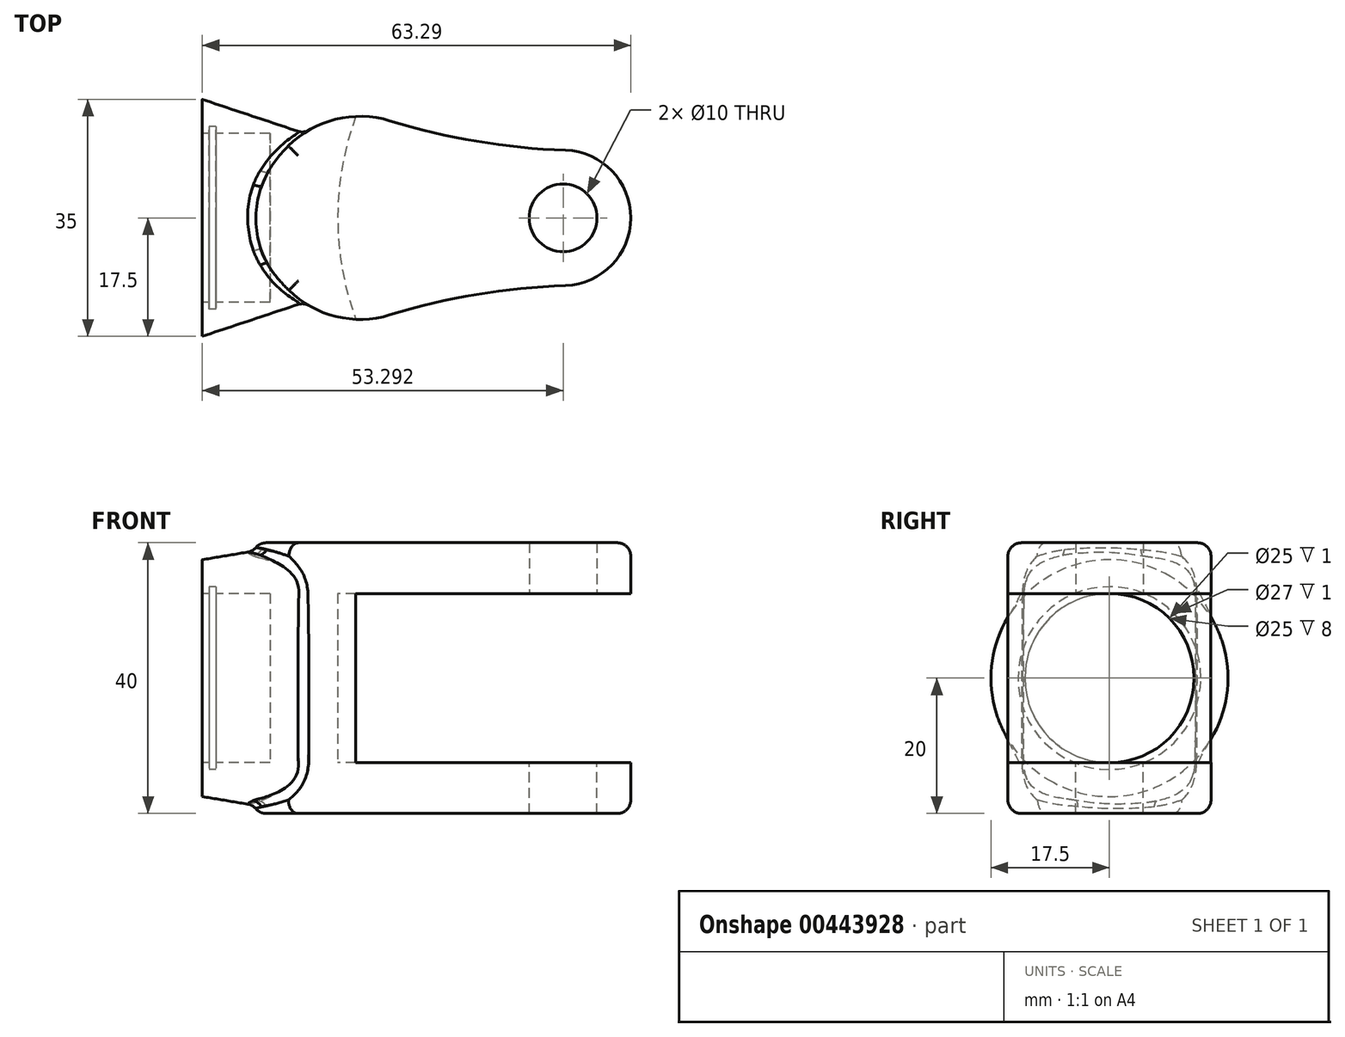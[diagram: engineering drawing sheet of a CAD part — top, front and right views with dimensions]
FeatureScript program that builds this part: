
annotation { "Feature Type Name" : "Feature", "Feature Type Description" : "" }
export const myFeature = defineFeature(function(context is Context, id is Id, definition is map)
    precondition{}
    {
        {
            var Q0;
            Q0=qCreatedBy(makeId("Right.planeOp"),FACE);
            var sketch = newSketch(context, id + "F0", { "sketchPlane" : qUnion([Q0])});
            skCircle(sketch, "E0", {"center": v(0, 0) * mm, "radius": 17.5 * mm});
            skSolve(sketch);
        }
        {
            var Q0;
            Q0=qCreatedBy(makeId("Right.planeOp"),FACE);
            cPlane(context, id + "F1", {"entities" : qUnion([Q0]), "cplaneType" : CPlaneType.OFFSET, "offset" : 15 * mm, "width" : 150 * mm, "height" : 150 * mm});
        }
        {
            var Q0;
            Q0=qCreatedBy(id+"F1.planeOp",FACE);
            var sketch = newSketch(context, id + "F2", { "sketchPlane" : qUnion([Q0])});
            skLineSegment(sketch, "E1.bottom", {"start": v(5, -20) * mm, "end": v(-5, -20) * mm});
            skLineSegment(sketch, "E1.top", {"start": v(5, 20) * mm, "end": v(-5, 20) * mm});
            skLineSegment(sketch, "E1.left", {"start": v(12.5, -12.5) * mm, "end": v(12.5, 12.5) * mm});
            skLineSegment(sketch, "E1.right", {"start": v(-12.5, -12.5) * mm, "end": v(-12.5, 12.5) * mm});
            skPoint(sketch, "E1.middle", {"position": v(0, 0) * mm});
            skPoint(sketch, "E2.visualSharp", {"position": v(-12.5, 20) * mm});
            skArc(sketch, "E2.filletArc", {"start": v(-5, 20) * mm, "mid": v(-10.3, 17.8) * mm, "end": v(-12.5, 12.5) * mm});
            skPoint(sketch, "E3.visualSharp", {"position": v(12.5, 20) * mm});
            skArc(sketch, "E3.filletArc", {"start": v(12.5, 12.5) * mm, "mid": v(10.3, 17.8) * mm, "end": v(5, 20) * mm});
            skPoint(sketch, "E4.visualSharp", {"position": v(12.5, -20) * mm});
            skArc(sketch, "E4.filletArc", {"start": v(5, -20) * mm, "mid": v(10.3, -17.8) * mm, "end": v(12.5, -12.5) * mm});
            skPoint(sketch, "E5.visualSharp", {"position": v(-12.5, -20) * mm});
            skArc(sketch, "E5.filletArc", {"start": v(-12.5, -12.5) * mm, "mid": v(-10.3, -17.8) * mm, "end": v(-5, -20) * mm});
            skSolve(sketch);
        }
        {
            var Q0;
            Q0 = qSketchRegion(id + "F2", true);
            var Q1;
            Q1 = qSketchRegion(id + "F0", true);
            loft(context, id + "F3", {"sheetProfilesArray" : [{ "sheetProfileEntities" : qUnion([Q0]) }, { "sheetProfileEntities" : qUnion([Q1]) }]});
        }
        {
            var Q0;
            Q0=qCreatedBy(makeId("Top.planeOp"),FACE);
            var sketch = newSketch(context, id + "F4", { "sketchPlane" : qUnion([Q0])});
            skCircle(sketch, "E6", {"center": v(23.3, 0) * mm, "radius": 15 * mm});
            skCircle(sketch, "E7", {"center": v(53.3, 0) * mm, "radius": 10 * mm});
            skArc(sketch, "E8", {"start": v(27.7, 14.34) * mm, "mid": v(40.52, 11.31) * mm, "end": v(53.63, 10) * mm});
            skArc(sketch, "E9.MirrorCS", {"start": v(27.7, -14.34) * mm, "mid": v(40.52, -11.31) * mm, "end": v(53.63, -10) * mm});
            skSolve(sketch);
        }
        {
            var Q0;
            Q0 = qSketchRegion(id + "F4", true);
            extrude(context, id + "F5", {"entities" : qUnion([Q0]), "operationType" : NewBodyOperationType.ADD, "endBound" : BoundingType.SYMMETRIC, "depth" : 40 * mm});
        }
        {
            var Q0;
            Q0=qCreatedBy(makeId("Front.planeOp"),FACE);
            var sketch = newSketch(context, id + "F6", { "sketchPlane" : qUnion([Q0])});
            skLineSegment(sketch, "E10.bottom", {"start": v(20, 12.5) * mm, "end": v(63.38, 12.5) * mm});
            skLineSegment(sketch, "E10.top", {"start": v(20, -12.5) * mm, "end": v(63.38, -12.5) * mm});
            skLineSegment(sketch, "E10.left", {"start": v(20, 12.5) * mm, "end": v(20, -12.5) * mm});
            skLineSegment(sketch, "E10.right", {"start": v(63.38, 12.5) * mm, "end": v(63.38, -12.5) * mm});
            skSolve(sketch);
        }
        {
            var Q0;
            Q0 = qSketchRegion(id + "F6", true);
            var Q1;
            Q1=sQuery(id+"F6.wireOp",EDGE,"E10.right");
            revolve(context, id + "F7", {"operationType" : NewBodyOperationType.REMOVE, "entities" : qUnion([Q0]), "axis" : qUnion([Q1]), "revolveType" : RevolveType.FULL, "oppositeDirection" : true});
        }
        {
            var Q0;
            Q0=makeQuery(id+"F3.opLoft","CAP_FACE",FACE,{"disambiguationData":[OSD([makeQuery(id+"F0.imprint","IMPRINT",FACE,{"disambiguationData":[TD([[makeQuery(id+"F0.imprint","IMPRINT",EDGE,{"derivedFrom":sQuery(id+"F0.wireOp",EDGE,"E0")}),1.0]])]})])],"isStart":true});
            var sketch = newSketch(context, id + "F8", { "sketchPlane" : qUnion([Q0])});
            skCircle(sketch, "E11", {"center": v(0, 0) * mm, "radius": 12.5 * mm});
            skSolve(sketch);
        }
        {
            var Q0;
            Q0 = qSketchRegion(id + "F8", true);
            extrude(context, id + "F9", {"entities" : qUnion([Q0]), "operationType" : NewBodyOperationType.REMOVE, "oppositeDirection" : true, "depth" : 10 * mm});
        }
        {
            var Q0;
            Q0=makeQuery(id+"F3.opLoft","CAP_FACE",FACE,{"disambiguationData":[OSD([makeQuery(id+"F0.imprint","IMPRINT",FACE,{"disambiguationData":[TD([[makeQuery(id+"F0.imprint","IMPRINT",EDGE,{"derivedFrom":sQuery(id+"F0.wireOp",EDGE,"E0")}),1.0]])]})])],"isStart":true});
            cPlane(context, id + "F10", {"entities" : qUnion([Q0]), "cplaneType" : CPlaneType.OFFSET, "offset" : 1 * mm, "oppositeDirection" : true, "width" : 150 * mm, "height" : 150 * mm});
        }
        {
            var Q0;
            Q0=qCreatedBy(id+"F10.planeOp",FACE);
            var sketch = newSketch(context, id + "F11", { "sketchPlane" : qUnion([Q0])});
            skCircle(sketch, "E12.0", {"center": v(0, 0) * mm, "radius": 13.5 * mm});
            skSolve(sketch);
        }
        {
            var Q0;
            Q0 = qSketchRegion(id + "F11", true);
            extrude(context, id + "F12", {"entities" : qUnion([Q0]), "operationType" : NewBodyOperationType.REMOVE, "oppositeDirection" : true, "depth" : 1 * mm});
        }
        {
            var Q0;
            Q0=qCreatedBy(makeId("Top.planeOp"),FACE);
            var sketch = newSketch(context, id + "F13", { "sketchPlane" : qUnion([Q0])});
            skCircle(sketch, "E13", {"center": v(53.3, 0) * mm, "radius": 5 * mm});
            skSolve(sketch);
        }
        {
            var Q0;
            Q0 = qSketchRegion(id + "F13", true);
            extrude(context, id + "F14", {"entities" : qUnion([Q0]), "operationType" : NewBodyOperationType.REMOVE, "endBound" : BoundingType.THROUGH_ALL, "oppositeDirection" : true, "depth" : 25 * mm});
        }
        {
            var Q0;
            Q0 = qSketchRegion(id + "F13", true);
            extrude(context, id + "F15", {"entities" : qUnion([Q0]), "operationType" : NewBodyOperationType.REMOVE, "endBound" : BoundingType.THROUGH_ALL, "depth" : 25 * mm});
        }
        {
            var Q0;
            Q0=makeQuery(id+"F3.opLoft","MID_CAP_EDGE",EDGE,{"disambiguationData":[OSD([sQuery(id+"F2.wireOp",EDGE,"E1.left"),sQuery(id+"F2.wireOp",EDGE,"E3.filletArc"),sQuery(id+"F2.wireOp",EDGE,"E4.filletArc")])],"capPos":0.0});
            var Q1;
            Q1=makeQuery(id+"F5.boolean.opBoolean","INTERSECT",EDGE,{"disambiguationData":[OD(1.0)],"derivedFrom":[makeQuery(id+"F3.opLoft","SWEPT_FACE",FACE,{"disambiguationData":[OSD([sQuery(id+"F0.wireOp",EDGE,"E0"),sQuery(id+"F2.wireOp",EDGE,"E1.bottom"),sQuery(id+"F2.wireOp",EDGE,"E4.filletArc"),sQuery(id+"F2.wireOp",EDGE,"E5.filletArc")])]}),makeQuery(id+"F5.opExtrude","SWEPT_FACE",FACE,{"disambiguationData":[OSD([sQuery(id+"F4.wireOp",EDGE,"E6")])]})]});
            var Q2;
            Q2=makeQuery(id+"F3.opLoft","MID_CAP_EDGE",EDGE,{"disambiguationData":[OSD([sQuery(id+"F2.wireOp",EDGE,"E1.right"),sQuery(id+"F2.wireOp",EDGE,"E2.filletArc"),sQuery(id+"F2.wireOp",EDGE,"E5.filletArc")])],"capPos":0.0});
            var Q3;
            Q3=makeQuery(id+"F5.boolean.opBoolean","INTERSECT",EDGE,{"disambiguationData":[OD(0.0)],"derivedFrom":[makeQuery(id+"F3.opLoft","SWEPT_FACE",FACE,{"disambiguationData":[OSD([sQuery(id+"F0.wireOp",EDGE,"E0"),sQuery(id+"F2.wireOp",EDGE,"E1.bottom"),sQuery(id+"F2.wireOp",EDGE,"E4.filletArc"),sQuery(id+"F2.wireOp",EDGE,"E5.filletArc")])]}),makeQuery(id+"F5.opExtrude","SWEPT_FACE",FACE,{"disambiguationData":[OSD([sQuery(id+"F4.wireOp",EDGE,"E6")])]})]});
            fillet(context, id + "F16", {"entities" : qUnion([Q0, Q1, Q2, Q3]), "radius" : 2 * mm, "tangentPropagation" : true, "allowEdgeOverflow" : false});
        }
        {
            var Q0;
            Q0=makeQuery(id+"F5.opExtrude","CAP_EDGE",EDGE,{"disambiguationData":[OSD([sQuery(id+"F4.wireOp",EDGE,"E6")])],"isStart":true});
            var Q1;
            Q1=makeQuery(id+"F5.opExtrude","CAP_EDGE",EDGE,{"disambiguationData":[OSD([sQuery(id+"F4.wireOp",EDGE,"E6")])],"isStart":false});
            var Q2;
            Q2=makeQuery(id+"F5.opExtrude","CAP_EDGE",EDGE,{"disambiguationData":[OSD([sQuery(id+"F4.wireOp",EDGE,"E6")])],"isStart":false});
            var Q3;
            Q3=makeQuery(id+"F5.opExtrude","CAP_EDGE",EDGE,{"disambiguationData":[OSD([sQuery(id+"F4.wireOp",EDGE,"E9.MirrorCS")])],"isStart":false});
            var Q4;
            Q4=makeQuery(id+"F5.opExtrude","CAP_EDGE",EDGE,{"disambiguationData":[OSD([sQuery(id+"F4.wireOp",EDGE,"E7")])],"isStart":false});
            var Q5;
            Q5=makeQuery(id+"F5.opExtrude","CAP_EDGE",EDGE,{"disambiguationData":[OSD([sQuery(id+"F4.wireOp",EDGE,"E8")])],"isStart":false});
            var Q6;
            {var subQ0=sQuery(id+"F4.wireOp",EDGE,"E6");Q6=makeQuery(id+"F16.opFillet","BLEND_EDGE",EDGE,{"blendedFrom":[makeQuery(id+"F5.boolean.opBoolean","INTERSECT",EDGE,{"disambiguationData":[OD(0.0)],"derivedFrom":[makeQuery(id+"F3.opLoft","SWEPT_FACE",FACE,{"disambiguationData":[OSD([sQuery(id+"F0.wireOp",EDGE,"E0"),sQuery(id+"F2.wireOp",EDGE,"E1.bottom"),sQuery(id+"F2.wireOp",EDGE,"E4.filletArc"),sQuery(id+"F2.wireOp",EDGE,"E5.filletArc")])]}),makeQuery(id+"F5.opExtrude","SWEPT_FACE",FACE,{"disambiguationData":[OSD([subQ0])]})]}),makeQuery(id+"F5.opExtrude","CAP_FACE",FACE,{"disambiguationData":[OSD([subQ0,sQuery(id+"F4.wireOp",EDGE,"E7"),sQuery(id+"F4.wireOp",EDGE,"E8"),sQuery(id+"F4.wireOp",EDGE,"E9.MirrorCS")])],"isStart":true})],"blendedInto":[makeQuery(id+"F5.opExtrude","CAP_FACE",FACE,{"disambiguationData":[OSD([subQ0,sQuery(id+"F4.wireOp",EDGE,"E7"),sQuery(id+"F4.wireOp",EDGE,"E8"),sQuery(id+"F4.wireOp",EDGE,"E9.MirrorCS")])],"isStart":true})]});}
            var Q7;
            Q7=makeQuery(id+"F5.opExtrude","CAP_EDGE",EDGE,{"disambiguationData":[OSD([sQuery(id+"F4.wireOp",EDGE,"E9.MirrorCS")])],"isStart":true});
            fillet(context, id + "F17", {"entities" : qUnion([Q0, Q1, Q2, Q3, Q4, Q5, Q6, Q7]), "radius" : 2 * mm, "tangentPropagation" : true, "allowEdgeOverflow" : false});
        }
    });
